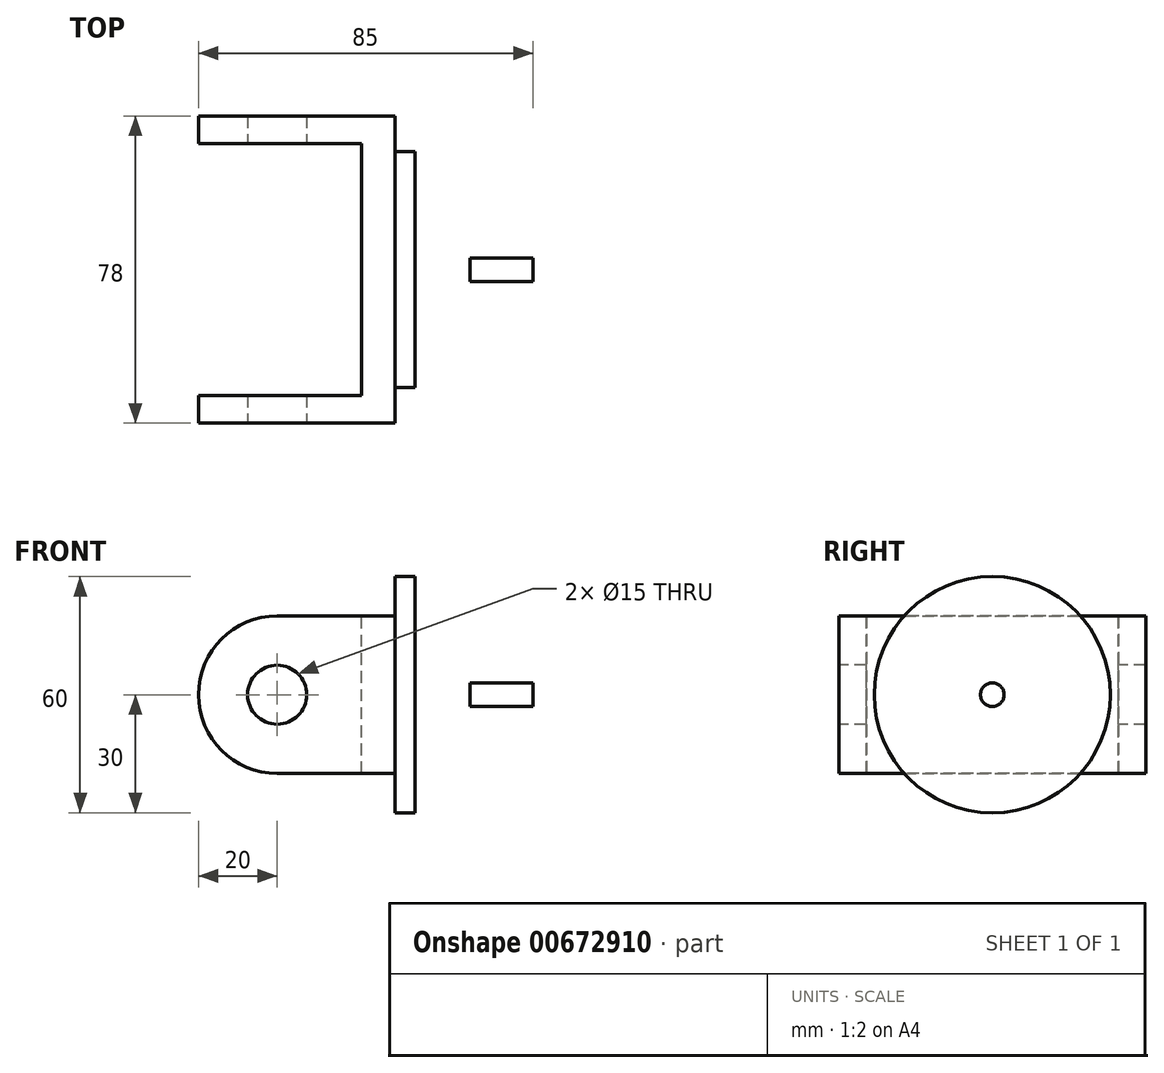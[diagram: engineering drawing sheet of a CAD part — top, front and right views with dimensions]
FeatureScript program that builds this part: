
annotation { "Feature Type Name" : "Feature", "Feature Type Description" : "" }
export const myFeature = defineFeature(function(context is Context, id is Id, definition is map)
    precondition{}
    {
        {
            var Q0;
            Q0=qCreatedBy(makeId("Front.planeOp"),FACE);
            var sketch = newSketch(context, id + "F0", { "sketchPlane" : qUnion([Q0])});
            skLineSegment(sketch, "E0.bottom", {"start": v(0, 0) * mm, "end": v(35, 0) * mm});
            skLineSegment(sketch, "E0.top", {"start": v(0, 7.5) * mm, "end": v(35, 7.5) * mm});
            skLineSegment(sketch, "E0.left", {"start": v(0, 0) * mm, "end": v(0, 7.5) * mm});
            skLineSegment(sketch, "E0.right", {"start": v(35, 0) * mm, "end": v(35, 7.5) * mm});
            skLineSegment(sketch, "E1.bottom", {"start": v(0, 0) * mm, "end": v(5, 0) * mm});
            skLineSegment(sketch, "E1.top", {"start": v(0, 30) * mm, "end": v(5, 30) * mm});
            skLineSegment(sketch, "E1.left", {"start": v(0, 0) * mm, "end": v(0, 30) * mm});
            skLineSegment(sketch, "E1.right", {"start": v(5, 0) * mm, "end": v(5, 30) * mm});
            skLineSegment(sketch, "E2.MirrorCS", {"start": v(0, 0) * mm, "end": v(0, -7.5) * mm});
            skLineSegment(sketch, "E3.MirrorCS", {"start": v(0, -7.5) * mm, "end": v(35, -7.5) * mm});
            skLineSegment(sketch, "E4.MirrorCS", {"start": v(35, 0) * mm, "end": v(35, -7.5) * mm});
            skLineSegment(sketch, "E5.MirrorCS", {"start": v(0, -30) * mm, "end": v(5, -30) * mm});
            skLineSegment(sketch, "E6.MirrorCS", {"start": v(0, 0) * mm, "end": v(0, -30) * mm});
            skLineSegment(sketch, "E7.MirrorCS", {"start": v(5, 0) * mm, "end": v(5, -30) * mm});
            skLineSegment(sketch, "E8.bottom", {"start": v(0, 20) * mm, "end": v(-30, 20) * mm});
            skLineSegment(sketch, "E8.top", {"start": v(0, -20) * mm, "end": v(-30, -20) * mm});
            skLineSegment(sketch, "E8.left", {"start": v(0, 20) * mm, "end": v(0, -20) * mm});
            skLineSegment(sketch, "E9", {"start": v(-30, 0) * mm, "end": v(0, 0) * mm});
            skCircle(sketch, "E10", {"center": v(-30, 0) * mm, "radius": 20 * mm});
            skLineSegment(sketch, "E11.bottom", {"start": v(19, 3) * mm, "end": v(35, 3) * mm});
            skLineSegment(sketch, "E11.top", {"start": v(19, 0) * mm, "end": v(35, 0) * mm});
            skLineSegment(sketch, "E11.left", {"start": v(19, 3) * mm, "end": v(19, 0) * mm});
            skLineSegment(sketch, "E11.right", {"start": v(35, 3) * mm, "end": v(35, 0) * mm});
            skLineSegment(sketch, "E12.MirrorCS", {"start": v(35, -3) * mm, "end": v(35, 0) * mm});
            skLineSegment(sketch, "E13.MirrorCS", {"start": v(19, -3) * mm, "end": v(35, -3) * mm});
            skLineSegment(sketch, "E14.MirrorCS", {"start": v(19, -3) * mm, "end": v(19, 0) * mm});
            skSolve(sketch);
        }
        {
            var Q0;
            {var subQ1=sQuery(id+"F0.wireOp",EDGE,"E0.bottom");Q0=makeQuery(id+"F0.imprint","IMPRINT",FACE,{"disambiguationData":[TD([[makeQuery(id+"F0.imprint","IMPRINT",EDGE,{"derivedFrom":subQ1}),1.0]])]});}
            var Q1;
            {var subQ5=sQuery(id+"F0.wireOp",EDGE,"E1.bottom");Q1=makeQuery(id+"F0.imprint","IMPRINT",FACE,{"disambiguationData":[TD([[makeQuery(id+"F0.imprint","IMPRINT",EDGE,{"derivedFrom":subQ5}),1.0]])]});}
            var Q2;
            {var subQ1=sQuery(id+"F0.wireOp",EDGE,"E1.top");Q2=makeQuery(id+"F0.imprint","IMPRINT",FACE,{"disambiguationData":[TD([[makeQuery(id+"F0.imprint","IMPRINT",EDGE,{"derivedFrom":subQ1}),-1.0]])]});}
            var Q3;
            Q3=sQuery(id+"F0.wireOp",EDGE,"E0.bottom");
            revolve(context, id + "F1", {"entities" : qUnion([Q0, Q1, Q2]), "axis" : qUnion([Q3]), "revolveType" : RevolveType.FULL});
        }
        {
            var Q0;
            {var subQ0=sQuery(id+"F0.wireOp",EDGE,"E10");var subQ1=makeQuery(id+"F0.imprint","INTERSECT",VERTEX,{"derivedFrom":[sQuery(id+"F0.wireOp",EDGE,"E8.bottom"),subQ0]});Q0=makeQuery(id+"F0.imprint","IMPRINT",FACE,{"disambiguationData":[TD([[makeQuery(id+"F0.imprint","IMPRINT",EDGE,{"disambiguationData":[TD([[subQ1,1.0]])],"derivedFrom":subQ0}),1.0]])]});}
            var Q1;
            {var subQ6=sQuery(id+"F0.wireOp",EDGE,"E8.bottom");Q1=makeQuery(id+"F0.imprint","IMPRINT",FACE,{"disambiguationData":[TD([[makeQuery(id+"F0.imprint","IMPRINT",EDGE,{"derivedFrom":subQ6}),1.0]])]});}
            var Q2;
            {var subQ2=sQuery(id+"F0.wireOp",EDGE,"E8.top");Q2=makeQuery(id+"F0.imprint","IMPRINT",FACE,{"disambiguationData":[TD([[makeQuery(id+"F0.imprint","IMPRINT",EDGE,{"derivedFrom":subQ2}),-1.0]])]});}
            extrude(context, id + "F2", {"entities" : qUnion([Q0, Q1, Q2]), "operationType" : NewBodyOperationType.ADD, "depth" : 78 * mm, "offsetDistance" : 25 * mm, "symmetric" : true});
        }
        {
            var Q0;
            Q0=qCreatedBy(makeId("Top.planeOp"),FACE);
            var sketch = newSketch(context, id + "F3", { "sketchPlane" : qUnion([Q0])});
            skLineSegment(sketch, "E15", {"start": v(-50, -39) * mm, "end": v(0, -39) * mm});
            skLineSegment(sketch, "E16", {"start": v(-50, 39) * mm, "end": v(0, 39) * mm});
            skLineSegment(sketch, "E17", {"start": v(-50, -39) * mm, "end": v(-50, 39) * mm});
            skLineSegment(sketch, "E18", {"start": v(0, 20) * mm, "end": v(0, 30) * mm});
            skLineSegment(sketch, "E19", {"start": v(0, -30) * mm, "end": v(0, -20) * mm});
            skLineSegment(sketch, "E20", {"start": v(5, -7.5) * mm, "end": v(35, -7.5) * mm});
            skLineSegment(sketch, "E21", {"start": v(35, 7.5) * mm, "end": v(5, 7.5) * mm});
            skLineSegment(sketch, "E22.bottom", {"start": v(-50, 32) * mm, "end": v(-8.55, 32) * mm});
            skLineSegment(sketch, "E22.top", {"start": v(-50, 0) * mm, "end": v(-8.55, 0) * mm});
            skLineSegment(sketch, "E22.left", {"start": v(-50, 32) * mm, "end": v(-50, 0) * mm});
            skLineSegment(sketch, "E22.right", {"start": v(-8.55, 32) * mm, "end": v(-8.55, 0) * mm});
            skLineSegment(sketch, "E23.MirrorCS", {"start": v(-8.55, -32) * mm, "end": v(-8.55, 0) * mm});
            skLineSegment(sketch, "E24.MirrorCS", {"start": v(-50, -32) * mm, "end": v(-50, 0) * mm});
            skLineSegment(sketch, "E25.MirrorCS", {"start": v(-50, -32) * mm, "end": v(-8.55, -32) * mm});
            skSolve(sketch);
        }
        {
            var Q0;
            Q0 = qSketchRegion(id + "F3", true);
            extrude(context, id + "F4", {"entities" : qUnion([Q0]), "operationType" : NewBodyOperationType.REMOVE, "oppositeDirection" : true, "depth" : 100 * mm, "offsetDistance" : 25 * mm, "symmetric" : true});
        }
        {
            var Q0;
            Q0=makeQuery(id+"F2.opExtrude","CAP_FACE",FACE,{"disambiguationData":[OSD([sQuery(id+"F0.wireOp",EDGE,"E8.bottom"),sQuery(id+"F0.wireOp",EDGE,"E8.top"),sQuery(id+"F0.wireOp",EDGE,"E8.left"),sQuery(id+"F0.wireOp",EDGE,"E10")])],"isStart":false});
            var sketch = newSketch(context, id + "F5", { "sketchPlane" : qUnion([Q0])});
            skArc(sketch, "E26.0.0", {"start": v(-30, 20) * mm, "mid": v(-50, 0) * mm, "end": v(-30, -20) * mm});
            skLineSegment(sketch, "E26.0.1", {"start": v(-30, -20) * mm, "end": v(0, -20) * mm});
            skLineSegment(sketch, "E26.0.2", {"start": v(0, -20) * mm, "end": v(0, 20) * mm});
            skLineSegment(sketch, "E26.0.3", {"start": v(0, 20) * mm, "end": v(-30, 20) * mm});
            skCircle(sketch, "E27", {"center": v(-30, 0) * mm, "radius": 7.5 * mm});
            skSolve(sketch);
        }
        {
            var Q0;
            Q0=makeQuery(id+"F5.imprint","IMPRINT",FACE,{"disambiguationData":[TD([[makeQuery(id+"F5.imprint","IMPRINT",EDGE,{"derivedFrom":sQuery(id+"F5.wireOp",EDGE,"E27")}),1.0]])]});
            extrude(context, id + "F6", {"entities" : qUnion([Q0]), "operationType" : NewBodyOperationType.REMOVE, "endBound" : BoundingType.THROUGH_ALL, "oppositeDirection" : true, "depth" : 25 * mm, "offsetDistance" : 25 * mm});
        }
    });
